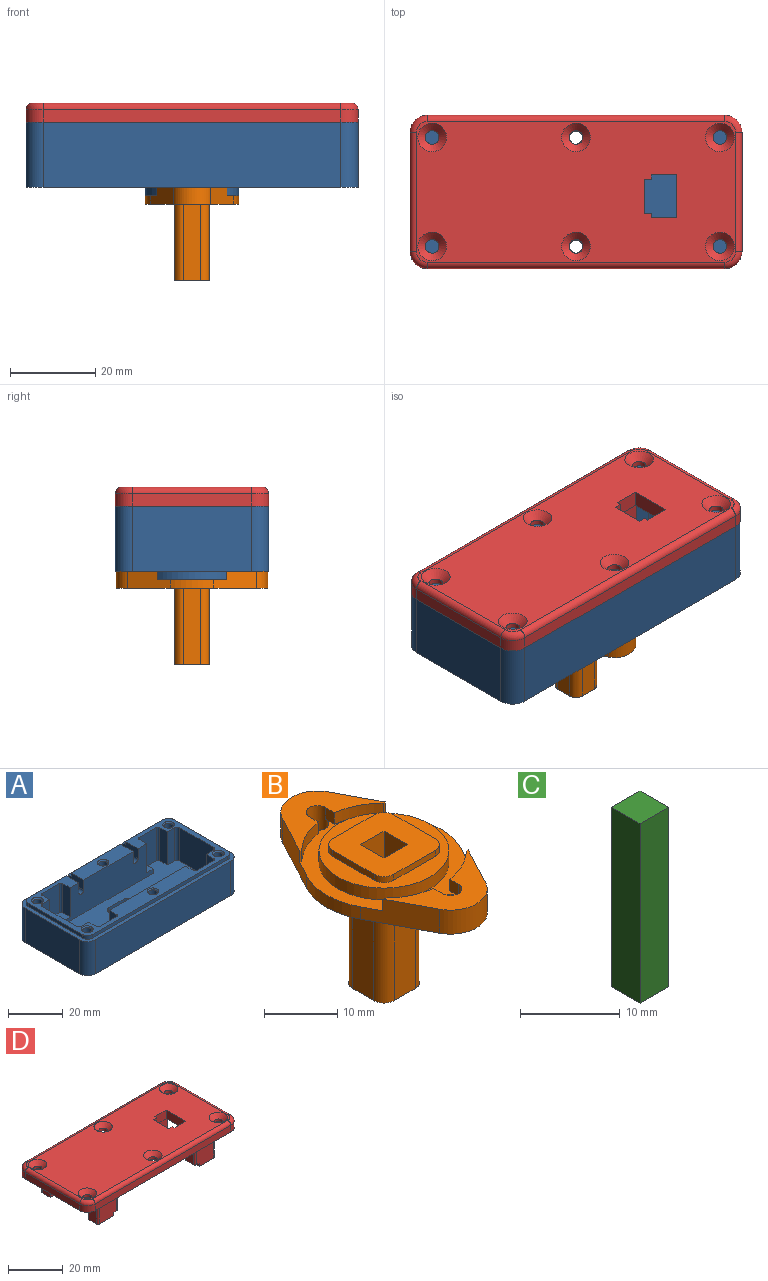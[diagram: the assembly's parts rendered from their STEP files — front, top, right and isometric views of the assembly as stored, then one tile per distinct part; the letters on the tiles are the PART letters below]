
ASSEMBLY  parts=4 mates=3
PART A: 98 faces, bbox 78x36x18.8 mm
  f0: plane 18x18mm, normal (0,0,-1), area 113.9mm2, adj f87,f88,f89,f90,f91,f92,f93,f94
  f1: plane 70.6x29.6mm, normal (0,0,1), area 1415.2mm2, adj f3,f4,f5,f6,f8,f17,f18,f19
  f2: plane 78x36mm, normal (0,0,-1), area 2397.5mm2, adj f53,f54,f55,f56,f57,f58,f59,f60
  f3: plane 46x14.8mm, normal (0,-1,0), area 567.6mm2, adj f1,f7,f13,f14,f15,f40,f41,f71
  f4: plane 14.8x3.7mm, normal (0,-1,0), area 54.8mm2, adj f1,f13,f18,f19
  f5: plane 14.8x3.7mm, normal (0,1,0), area 54.8mm2, adj f1,f13,f21,f23
  f6: plane 46x14.8mm, normal (0,1,0), area 595mm2, adj f1,f13,f16,f27,f28,f44,f83,f84
  f7: plane 25.5x6.45mm, normal (0,0,1), area 150.3mm2, adj f3,f10,f71,f76,f78
  f8: plane 14.8x3.7mm, normal (0,-1,0), area 54.8mm2, adj f1,f13,f35,f36
  f9: plane 19.75x1.5mm, normal (0,1,0), area 29.6mm2, adj f11,f13,f47,f74
  f10: plane 25.5x1.5mm, normal (0,1,0), area 38.2mm2, adj f7,f12,f71,f76
  f11: plane 78x36mm, normal (0,0,1), area 278.9mm2, adj f9,f45,f46,f47,f48,f49,f50,f51
  f12: plane 25.5x1.5mm, normal (0,0,1), area 38.2mm2, adj f10,f58,f71,f76
  f13: plane 75x33mm, normal (0,0,1), area 584.1mm2, adj f3,f4,f5,f6,f8,f9,f17,f18
  f14: plane 4.75x3.3mm, normal (0,0,1), area 15.5mm2, adj f3,f41,f42,f43,f86
  f15: plane 4.75x3.3mm, normal (0,0,1), area 15.5mm2, adj f3,f38,f39,f40,f85
  f16: plane 4.75x3.3mm, normal (0,0,1), area 15.5mm2, adj f6,f25,f26,f27,f84
  f17: cylinder r=0.8mm len=14.8mm, axis (0,0,1), area 18.6mm2, adj f1,f13,f18,f43
  f18: plane 14.8x3.95mm, normal (1,0,0), area 58.5mm2, adj f1,f4,f13,f17
  f19: cylinder r=1.3mm len=14.8mm, axis (0,0,1), area 30.2mm2, adj f1,f4,f13,f20
  f20: plane 17.5x14.8mm, normal (1,0,0), area 259mm2, adj f1,f13,f19,f21
  f21: cylinder r=1.3mm len=14.8mm, axis (0,0,1), area 30.2mm2, adj f1,f5,f13,f20
  f22: plane 14.8x3.7mm, normal (0,1,0), area 54.8mm2, adj f1,f13,f32,f33
  f23: plane 14.8x3.95mm, normal (1,0,0), area 58.5mm2, adj f1,f5,f13,f24
  f24: cylinder r=0.8mm len=14.8mm, axis (0,0,1), area 18.6mm2, adj f1,f13,f23,f25
  f25: plane 14.8x9mm, normal (0,1,0), area 128.7mm2, adj f1,f13,f16,f24,f26,f84
  f26: cylinder r=0.8mm len=13mm, axis (0,0,1), area 16.3mm2, adj f13,f16,f25,f27
  f27: plane 13x3.95mm, normal (-1,0,0), area 51.4mm2, adj f6,f13,f16,f26
  f28: plane 13x3.95mm, normal (1,0,0), area 51.4mm2, adj f6,f13,f29,f44
  f29: cylinder r=0.8mm len=13mm, axis (0,0,1), area 16.3mm2, adj f13,f28,f30,f44
  f30: plane 14.8x9mm, normal (0,1,0), area 128.7mm2, adj f1,f13,f29,f31,f44,f83
  f31: cylinder r=0.8mm len=14.8mm, axis (0,0,1), area 18.6mm2, adj f1,f13,f30,f32
  f32: plane 14.8x3.95mm, normal (-1,0,0), area 58.5mm2, adj f1,f13,f22,f31
  f33: cylinder r=1.3mm len=14.8mm, axis (0,0,1), area 30.2mm2, adj f1,f13,f22,f34
  f34: plane 17.5x14.8mm, normal (-1,0,0), area 259mm2, adj f1,f13,f33,f35
  f35: cylinder r=1.3mm len=14.8mm, axis (0,0,1), area 30.2mm2, adj f1,f8,f13,f34
  f36: plane 14.8x3.95mm, normal (-1,0,0), area 58.5mm2, adj f1,f8,f13,f37
  f37: cylinder r=0.8mm len=14.8mm, axis (0,0,1), area 18.6mm2, adj f1,f13,f36,f38
  f38: plane 14.8x9mm, normal (0,-1,0), area 128.7mm2, adj f1,f13,f15,f37,f39,f85
  f39: cylinder r=0.8mm len=13mm, axis (0,0,1), area 16.3mm2, adj f13,f15,f38,f40
  f40: plane 13x3.95mm, normal (1,0,0), area 51.4mm2, adj f3,f13,f15,f39
  f41: plane 13x3.95mm, normal (-1,0,0), area 51.4mm2, adj f3,f13,f14,f42
  f42: cylinder r=0.8mm len=13mm, axis (0,0,1), area 16.3mm2, adj f13,f14,f41,f43
  f43: plane 14.8x9mm, normal (0,-1,0), area 128.7mm2, adj f1,f13,f14,f17,f42,f86
  f44: plane 4.75x3.3mm, normal (0,0,1), area 15.5mm2, adj f6,f28,f29,f30,f83
  f45: cylinder r=2.5mm len=2.5mm, axis (0,0,1), area 5.9mm2, adj f11,f13,f46,f52
  f46: plane 19.75x1.5mm, normal (0,1,0), area 29.6mm2, adj f11,f13,f45,f73
  f47: cylinder r=2.5mm len=2.5mm, axis (0,0,1), area 5.9mm2, adj f9,f11,f13,f48
  f48: plane 28x1.5mm, normal (1,0,0), area 42mm2, adj f11,f13,f47,f49
  f49: cylinder r=2.5mm len=2.5mm, axis (0,0,1), area 5.9mm2, adj f11,f13,f48,f50
  f50: plane 70x1.5mm, normal (0,-1,0), area 105mm2, adj f11,f13,f49,f51
  f51: cylinder r=2.5mm len=2.5mm, axis (0,0,1), area 5.9mm2, adj f11,f13,f50,f52
  f52: plane 28x1.5mm, normal (-1,0,0), area 42mm2, adj f11,f13,f45,f51
  f53: cylinder r=4mm len=15.3mm, axis (0,0,-1), area 96.1mm2, adj f2,f11,f54,f60
  f54: plane 70x15.3mm, normal (0,-1,0), area 1071mm2, adj f2,f11,f53,f55
  f55: cylinder r=4mm len=15.3mm, axis (0,0,-1), area 96.1mm2, adj f2,f11,f54,f56
  f56: plane 28x15.3mm, normal (-1,0,0), area 428.4mm2, adj f2,f11,f55,f57
  f57: cylinder r=4mm len=15.3mm, axis (0,0,-1), area 96.1mm2, adj f2,f11,f56,f58
  f58: plane 70x15.3mm, normal (0,1,0), area 1051.1mm2, adj f2,f11,f12,f57,f59,f71,f72,f73
  f59: cylinder r=4mm len=15.3mm, axis (0,0,-1), area 96.1mm2, adj f2,f11,f58,f60
  f60: plane 28x15.3mm, normal (1,0,0), area 428.4mm2, adj f2,f11,f53,f59
  f61: cylinder r=1.62mm len=5.5mm, axis (0,0,1), area 56.2mm2, adj f62,f81
  f62: plane 3.25x3.25mm, normal (0,0,1), area 8.3mm2, adj f61
  f63: cylinder r=1.62mm len=5.5mm, axis (0,0,1), area 56.2mm2, adj f64,f82
  f64: plane 3.25x3.25mm, normal (0,0,1), area 8.3mm2, adj f63
  f65: cylinder r=1.62mm len=5.5mm, axis (0,0,1), area 56.2mm2, adj f66,f79
  f66: plane 3.25x3.25mm, normal (0,0,1), area 8.3mm2, adj f65
  f67: cylinder r=1.62mm len=5.5mm, axis (0,0,1), area 56.2mm2, adj f68,f80
  f68: plane 3.25x3.25mm, normal (0,0,1), area 8.3mm2, adj f67
  f69: cylinder r=1.62mm len=16.3mm, axis (0,0,1), area 166.4mm2, adj f2,f77
  f70: cylinder r=1.62mm len=16.3mm, axis (0,0,1), area 166.4mm2, adj f2,f78
  f71: plane 7.95x4.5mm, normal (-1,0,0), area 33.5mm2, adj f3,f7,f10,f12,f58,f72
  f72: cylinder r=1.25mm len=7.95mm, axis (0,1,0), area 31.2mm2, adj f3,f58,f71,f73
  f73: plane 7.95x4.5mm, normal (1,0,0), area 33.5mm2, adj f3,f11,f13,f46,f58,f72
  f74: plane 7.95x4.5mm, normal (-1,0,0), area 33.5mm2, adj f3,f9,f11,f13,f58,f75
  f75: cylinder r=1.25mm len=7.95mm, axis (0,1,0), area 31.2mm2, adj f3,f58,f74,f76
  f76: plane 7.95x4.5mm, normal (1,0,0), area 33.5mm2, adj f3,f7,f10,f12,f58,f75
  f77: cone r=1.62mm half-angle=45deg, axis (0,0,1), area 8.3mm2, adj f13,f69
  f78: cone r=1.62mm half-angle=45deg, axis (0,0,1), area 8.3mm2, adj f7,f70
  f79: cone r=1.62mm half-angle=45deg, axis (0,0,1), area 8.3mm2, adj f13,f65
  f80: cone r=1.62mm half-angle=45deg, axis (0,0,1), area 8.3mm2, adj f13,f67
  f81: cone r=1.62mm half-angle=45deg, axis (0,0,1), area 8.3mm2, adj f13,f61
  f82: cone r=1.62mm half-angle=45deg, axis (0,0,1), area 8.3mm2, adj f13,f63
  f83: plane 4.75x1.8mm, normal (1,0,0), area 8.6mm2, adj f1,f6,f30,f44
  f84: plane 4.75x1.8mm, normal (-1,0,0), area 8.6mm2, adj f1,f6,f16,f25
  f85: plane 4.75x1.8mm, normal (1,0,0), area 8.6mm2, adj f1,f3,f15,f38
  f86: plane 4.75x1.8mm, normal (-1,0,0), area 8.6mm2, adj f1,f3,f14,f43
  f87: plane 8x2mm, normal (0,1,0), area 16mm2, adj f0,f1,f88,f94
  f88: cylinder r=2mm len=2mm, axis (0,0,-1), area 6.3mm2, adj f0,f1,f87,f89
  f89: plane 8x2mm, normal (-1,0,0), area 16mm2, adj f0,f1,f88,f90
  f90: cylinder r=2mm len=2mm, axis (0,0,-1), area 6.3mm2, adj f0,f1,f89,f91
  f91: plane 8x2mm, normal (0,-1,0), area 16mm2, adj f0,f1,f90,f92
  f92: cylinder r=2mm len=2mm, axis (0,0,-1), area 6.3mm2, adj f0,f1,f91,f93
  f93: plane 8x2mm, normal (1,0,0), area 16mm2, adj f0,f1,f92,f94
  f94: cylinder r=2mm len=2mm, axis (0,0,-1), area 6.3mm2, adj f0,f1,f87,f93
  f95: cylinder r=9mm len=18mm, axis (0,0,1), area 113.1mm2, adj f0,f97
  f96: cylinder r=11mm len=22mm, axis (0,0,1), area 138.2mm2, adj f2,f97
  f97: plane 22x22mm, normal (0,0,-1), area 125.7mm2, adj f95,f96
PART B: 51 faces, bbox 22x35.6x23 mm
  f0: plane 16.42x9.8mm, normal (0,0,1), area 63.5mm2, adj f1,f6,f7,f39,f40,f41,f42,f46
  f1: cylinder r=11.2mm len=6.29mm, axis (0,0,1), area 13.9mm2, adj f0,f22,f40,f50
  f2: cylinder r=11.2mm len=6.29mm, axis (0,0,1), area 13.9mm2, adj f5,f22,f44,f47
  f3: cylinder r=1.55mm len=4mm, axis (0,0,-1), area 29.5mm2, adj f5,f11,f22,f47,f48
  f4: plane 9.99x5.3mm, normal (-0.88,-0.47,0), area 38.9mm2, adj f5,f10,f11,f22,f38,f44
  f5: plane 16.42x9.8mm, normal (0,0,1), area 63.5mm2, adj f2,f3,f4,f37,f38,f43,f44,f45
  f6: plane 9.99x5.3mm, normal (0.88,0.47,0), area 38.9mm2, adj f0,f8,f11,f22,f39,f40
  f7: plane 9.99x5.3mm, normal (-0.88,0.47,0), area 38.9mm2, adj f0,f10,f11,f22,f39,f42
  f8: cylinder r=11mm len=10.31mm, axis (0,0,1), area 22mm2, adj f6,f11,f22,f37
  f9: plane 11.8x11.8mm, normal (0,0,1), area 116.3mm2, adj f24,f25,f26,f27,f28,f29,f30,f31
  f10: cylinder r=11mm len=10.31mm, axis (0,0,1), area 22mm2, adj f4,f7,f11,f22
  f11: plane 35.6x22mm, normal (0,0,-1), area 458.4mm2, adj f3,f4,f6,f7,f8,f10,f12,f13
  f12: plane 18x4mm, normal (0,-1,0), area 72mm2, adj f11,f13,f19,f20
  f13: cylinder r=2mm len=18mm, axis (0,0,1), area 56.5mm2, adj f11,f12,f14,f20
  f14: plane 18x4mm, normal (-1,0,0), area 72mm2, adj f11,f13,f15,f20
  f15: cylinder r=2mm len=18mm, axis (0,0,1), area 56.5mm2, adj f11,f14,f16,f20
  f16: plane 18x4mm, normal (0,1,0), area 72mm2, adj f11,f15,f17,f20
  f17: cylinder r=2mm len=18mm, axis (0,0,1), area 56.5mm2, adj f11,f16,f18,f20
  f18: plane 18x4mm, normal (1,0,0), area 72mm2, adj f11,f17,f19,f20
  f19: cylinder r=2mm len=18mm, axis (0,0,1), area 56.5mm2, adj f11,f12,f18,f20
  f20: plane 8x8mm, normal (0,0,-1), area 60.6mm2, adj f12,f13,f14,f15,f16,f17,f18,f19
  f21: cylinder r=8.85mm len=17.7mm, axis (0,0,1), area 108.4mm2, adj f22,f23
  f22: plane 25.6x22mm, normal (0,0,1), area 145.8mm2, adj f1,f2,f3,f4,f6,f7,f8,f10
  f23: plane 17.7x17.7mm, normal (0,0,1), area 109.9mm2, adj f21,f24,f25,f26,f27,f28,f29,f30
  f24: plane 8x1mm, normal (-1,0,0), area 8mm2, adj f9,f23,f25,f31
  f25: cylinder r=1.9mm len=1.9mm, axis (0,0,-1), area 3mm2, adj f9,f23,f24,f26
  f26: plane 8x1mm, normal (0,-1,0), area 8mm2, adj f9,f23,f25,f27
  f27: cylinder r=1.9mm len=1.9mm, axis (0,0,-1), area 3mm2, adj f9,f23,f26,f28
  f28: plane 8x1mm, normal (1,0,0), area 8mm2, adj f9,f23,f27,f29
  f29: cylinder r=1.9mm len=1.9mm, axis (0,0,-1), area 3mm2, adj f9,f23,f28,f30
  f30: plane 8x1mm, normal (0,1,0), area 8mm2, adj f9,f23,f29,f31
  f31: cylinder r=1.9mm len=1.9mm, axis (0,0,-1), area 3mm2, adj f9,f23,f24,f30
  f32: plane 4.45x4.45mm, normal (0,0,1), area 19.8mm2, adj f33,f34,f35,f36
  f33: plane 21x4.45mm, normal (0,1,0), area 93.4mm2, adj f9,f32,f34,f36
  f34: plane 21x4.45mm, normal (-1,0,0), area 93.4mm2, adj f9,f32,f33,f35
  f35: plane 21x4.45mm, normal (0,-1,0), area 93.4mm2, adj f9,f32,f34,f36
  f36: plane 21x4.45mm, normal (1,0,0), area 93.4mm2, adj f9,f32,f33,f35
  f37: plane 9.99x5.3mm, normal (0.88,-0.47,0), area 38.9mm2, adj f5,f8,f11,f22,f38,f43
  f38: cylinder r=5mm len=8.83mm, axis (0,0,1), area 43.3mm2, adj f4,f5,f11,f37
  f39: cylinder r=5mm len=8.83mm, axis (0,0,1), area 43.3mm2, adj f0,f6,f7,f11
  f40: plane 1.95x0.37mm, normal (0,-1,0), area 0.7mm2, adj f0,f1,f6,f22
  f41: cylinder r=11.2mm len=6.29mm, axis (0,0,1), area 13.9mm2, adj f0,f22,f42,f49
  f42: plane 1.95x0.37mm, normal (0,-1,0), area 0.7mm2, adj f0,f7,f22,f41
  f43: plane 1.95x0.37mm, normal (0,1,0), area 0.7mm2, adj f5,f22,f37,f45
  f44: plane 1.95x0.37mm, normal (0,1,0), area 0.7mm2, adj f2,f4,f5,f22
  f45: cylinder r=11.2mm len=6.29mm, axis (0,0,1), area 13.9mm2, adj f5,f22,f43,f48
  f46: cylinder r=1.55mm len=4mm, axis (0,0,-1), area 29.5mm2, adj f0,f11,f22,f49,f50
  f47: plane 1.95x1.71mm, normal (1,0,0), area 3.3mm2, adj f2,f3,f5,f22
  f48: plane 1.95x1.71mm, normal (-1,0,0), area 3.3mm2, adj f3,f5,f22,f45
  f49: plane 1.95x1.71mm, normal (1,0,0), area 3.3mm2, adj f0,f22,f41,f46
  f50: plane 1.95x1.71mm, normal (-1,0,0), area 3.3mm2, adj f0,f1,f22,f46
PART C: 6 faces, bbox 4x4x22 mm
  f0: plane 22x4mm, normal (-1,0,0), area 88mm2, adj f1,f3,f4,f5
  f1: plane 22x4mm, normal (0,-1,0), area 88mm2, adj f0,f2,f4,f5
  f2: plane 22x4mm, normal (1,0,0), area 88mm2, adj f1,f3,f4,f5
  f3: plane 22x4mm, normal (0,1,0), area 88mm2, adj f0,f2,f4,f5
  f4: plane 4x4mm, normal (0,0,-1), area 16mm2, adj f0,f1,f2,f3
  f5: plane 4x4mm, normal (0,0,1), area 16mm2, adj f0,f1,f2,f3
PART D: 100 faces, bbox 78.7x36.7x15 mm
  f0: plane 70.4x19.9mm, normal (0,0,-1), area 1284.5mm2, adj f3,f4,f6,f7,f27,f29,f31,f32
  f1: plane 75x33mm, normal (0,0,1), area 2183.2mm2, adj f55,f56,f57,f58,f59,f60,f61,f62
  f2: plane 12x9mm, normal (0,1,0), area 105.7mm2, adj f11,f14,f26,f28,f86,f87
  f3: plane 10.5x5.05mm, normal (1,0,0), area 43mm2, adj f0,f10,f14,f26,f29,f53,f87
  f4: plane 10.5x5.05mm, normal (-1,0,0), area 43mm2, adj f0,f15,f26,f29,f49,f54,f89
  f5: plane 12x9mm, normal (0,1,0), area 105.7mm2, adj f15,f26,f30,f50,f88,f89
  f6: plane 10.5x5.05mm, normal (-1,0,0), area 43mm2, adj f0,f9,f16,f26,f40,f52,f91
  f7: plane 10.5x5.05mm, normal (1,0,0), area 43mm2, adj f0,f12,f17,f26,f40,f51,f85
  f8: plane 12x9mm, normal (0,-1,0), area 105.7mm2, adj f13,f17,f26,f41,f84,f85
  f9: plane 10.4x10.2mm, normal (0,1,0), area 102.8mm2, adj f6,f37,f48,f52,f90,f91
  f10: plane 10.4x10.2mm, normal (0,-1,0), area 102.8mm2, adj f3,f11,f27,f53,f86,f87
  f11: plane 8.2x4.75mm, normal (0,0,-1), area 38.8mm2, adj f2,f10,f27,f28,f86
  f12: plane 10.4x10.2mm, normal (0,1,0), area 102.8mm2, adj f7,f13,f42,f51,f84,f85
  f13: plane 8.2x4.75mm, normal (0,0,-1), area 38.8mm2, adj f8,f12,f41,f42,f84
  f14: cylinder r=0.7mm len=10.5mm, axis (0,0,1), area 11.5mm2, adj f2,f3,f26,f87
  f15: cylinder r=0.7mm len=10.5mm, axis (0,0,1), area 11.5mm2, adj f4,f5,f26,f89
  f16: cylinder r=0.7mm len=10.5mm, axis (0,0,1), area 11.5mm2, adj f6,f26,f39,f91
  f17: cylinder r=0.7mm len=10.5mm, axis (0,0,1), area 11.5mm2, adj f7,f8,f26,f85
  f18: cylinder r=4mm len=4mm, axis (0,0,1), area 18.8mm2, adj f19,f25,f61,f83
  f19: plane 70x3mm, normal (0,1,0), area 210mm2, adj f18,f20,f59,f83
  f20: cylinder r=4mm len=4mm, axis (0,0,1), area 18.8mm2, adj f19,f21,f57,f83
  f21: plane 28x3mm, normal (-1,0,0), area 84mm2, adj f20,f22,f55,f83
  f22: cylinder r=4mm len=4mm, axis (0,0,1), area 18.8mm2, adj f21,f23,f56,f83
  f23: plane 70x3mm, normal (0,-1,0), area 210mm2, adj f22,f24,f58,f83
  f24: cylinder r=4mm len=4mm, axis (0,0,1), area 18.8mm2, adj f23,f25,f60,f83
  f25: plane 28x3mm, normal (1,0,0), area 84mm2, adj f18,f24,f62,f83
  f26: plane 75.1x33.1mm, normal (0,0,-1), area 835.5mm2, adj f2,f3,f4,f5,f6,f7,f8,f14
  f27: plane 12x5.05mm, normal (-1,0,0), area 49.1mm2, adj f0,f10,f11,f26,f28,f47,f53
  f28: cylinder r=0.7mm len=12mm, axis (0,0,1), area 13.2mm2, adj f2,f11,f26,f27
  f29: plane 39.6x0.8mm, normal (0,1,0), area 31.7mm2, adj f0,f3,f4,f26
  f30: cylinder r=0.7mm len=12mm, axis (0,0,1), area 13.2mm2, adj f5,f26,f31,f50
  f31: plane 12x5.05mm, normal (1,0,0), area 49.1mm2, adj f0,f26,f30,f32,f49,f50,f54
  f32: plane 3.8x0.8mm, normal (0,1,0), area 3mm2, adj f0,f26,f31,f33
  f33: cylinder r=1.2mm len=1.2mm, axis (0,0,1), area 1.5mm2, adj f0,f26,f32,f34
  f34: plane 17.5x0.8mm, normal (1,0,0), area 14mm2, adj f0,f26,f33,f35
  f35: cylinder r=1.2mm len=1.2mm, axis (0,0,1), area 1.5mm2, adj f0,f26,f34,f36
  f36: plane 3.8x0.8mm, normal (0,-1,0), area 3mm2, adj f0,f26,f35,f37
  f37: plane 12x5.05mm, normal (1,0,0), area 49.1mm2, adj f0,f9,f26,f36,f38,f48,f52
  f38: cylinder r=0.7mm len=12mm, axis (0,0,1), area 13.2mm2, adj f26,f37,f39,f48
  f39: plane 12x9mm, normal (0,-1,0), area 105.7mm2, adj f16,f26,f38,f48,f90,f91
  f40: plane 39.6x0.8mm, normal (0,-1,0), area 31.7mm2, adj f0,f6,f7,f26
  f41: cylinder r=0.7mm len=12mm, axis (0,0,1), area 13.2mm2, adj f8,f13,f26,f42
  f42: plane 12x5.05mm, normal (-1,0,0), area 49.1mm2, adj f0,f12,f13,f26,f41,f43,f51
  f43: plane 3.8x0.8mm, normal (0,-1,0), area 3mm2, adj f0,f26,f42,f44
  f44: cylinder r=1.2mm len=1.2mm, axis (0,0,1), area 1.5mm2, adj f0,f26,f43,f45
  f45: plane 17.5x0.8mm, normal (-1,0,0), area 14mm2, adj f0,f26,f44,f46
  f46: cylinder r=1.2mm len=1.2mm, axis (0,0,1), area 1.5mm2, adj f0,f26,f45,f47
  f47: plane 3.8x0.8mm, normal (0,1,0), area 3mm2, adj f0,f26,f27,f46
  f48: plane 8.2x4.75mm, normal (0,0,-1), area 38.8mm2, adj f9,f37,f38,f39,f90
  f49: plane 10.4x10.2mm, normal (0,-1,0), area 102.8mm2, adj f4,f31,f50,f54,f88,f89
  f50: plane 8.2x4.75mm, normal (0,0,-1), area 38.8mm2, adj f5,f30,f31,f49,f88
  f51: plane 10.4x1mm, normal (0,0.71,-0.71), area 14.7mm2, adj f0,f7,f12,f42
  f52: plane 10.4x1mm, normal (0,0.71,-0.71), area 14.7mm2, adj f0,f6,f9,f37
  f53: plane 10.4x1mm, normal (0,-0.71,-0.71), area 14.7mm2, adj f0,f3,f10,f27
  f54: plane 10.4x1mm, normal (0,-0.71,-0.71), area 14.7mm2, adj f0,f4,f31,f49
  f55: cylinder r=1.5mm len=28mm, axis (0,-1,0), area 66mm2, adj f1,f21,f56,f57
  f56: torus R=2.5mm, axis (0,0,1), area 12.8mm2, adj f1,f22,f55,f58
  f57: torus R=2.5mm, axis (0,0,1), area 12.8mm2, adj f1,f20,f55,f59
  f58: cylinder r=1.5mm len=70mm, axis (1,0,0), area 164.9mm2, adj f1,f23,f56,f60
  f59: cylinder r=1.5mm len=70mm, axis (-1,0,0), area 164.9mm2, adj f1,f19,f57,f61
  f60: torus R=2.5mm, axis (0,0,1), area 12.8mm2, adj f1,f24,f58,f62
  f61: torus R=2.5mm, axis (0,0,1), area 12.8mm2, adj f1,f18,f59,f62
  f62: cylinder r=1.5mm len=28mm, axis (0,1,0), area 66mm2, adj f1,f25,f60,f61
  f63: cylinder r=1.6mm len=3.2mm, axis (0,0,1), area 12.5mm2, adj f26,f64
  f64: cone r=1.6mm half-angle=45deg, axis (0,0,1), area 38.8mm2, adj f1,f63
  f65: cylinder r=1.6mm len=3.2mm, axis (0,0,1), area 12.5mm2, adj f26,f66
  f66: cone r=1.6mm half-angle=45deg, axis (0,0,1), area 38.8mm2, adj f1,f65
  f67: cylinder r=1.6mm len=3.2mm, axis (0,0,1), area 12.5mm2, adj f26,f68
  f68: cone r=1.6mm half-angle=45deg, axis (0,0,1), area 38.8mm2, adj f1,f67
  f69: cylinder r=1.6mm len=3.2mm, axis (0,0,1), area 12.5mm2, adj f26,f70
  f70: cone r=1.6mm half-angle=45deg, axis (0,0,1), area 38.8mm2, adj f1,f69
  f71: cylinder r=1.6mm len=3.2mm, axis (0,0,1), area 12.5mm2, adj f26,f72
  f72: cone r=1.6mm half-angle=45deg, axis (0,0,1), area 38.8mm2, adj f1,f71
  f73: cylinder r=1.6mm len=3.2mm, axis (0,0,1), area 12.5mm2, adj f26,f74
  f74: cone r=1.6mm half-angle=45deg, axis (0,0,1), area 38.8mm2, adj f1,f73
  f75: cylinder r=2.55mm len=2.55mm, axis (0,0,1), area 6mm2, adj f26,f76,f82,f83
  f76: plane 70x1.5mm, normal (0,-1,0), area 105mm2, adj f26,f75,f77,f83
  f77: cylinder r=2.55mm len=2.55mm, axis (0,0,1), area 6mm2, adj f26,f76,f78,f83
  f78: plane 28x1.5mm, normal (1,0,0), area 42mm2, adj f26,f77,f79,f83
  f79: cylinder r=2.55mm len=2.55mm, axis (0,0,1), area 6mm2, adj f26,f78,f80,f83
  f80: plane 70x1.5mm, normal (0,1,0), area 105mm2, adj f26,f79,f81,f83
  f81: cylinder r=2.55mm len=2.55mm, axis (0,0,1), area 6mm2, adj f26,f80,f82,f83
  f82: plane 28x1.5mm, normal (-1,0,0), area 42mm2, adj f26,f75,f81,f83
  f83: plane 78x36mm, normal (0,0,-1), area 314mm2, adj f18,f19,f20,f21,f22,f23,f24,f25
  f84: plane 4.75x1.5mm, normal (1,0,0), area 7.1mm2, adj f8,f12,f13,f85
  f85: plane 4.75x2.2mm, normal (0,0,-1), area 10.3mm2, adj f7,f8,f12,f17,f84
  f86: plane 4.75x1.5mm, normal (1,0,0), area 7.1mm2, adj f2,f10,f11,f87
  f87: plane 4.75x2.2mm, normal (0,0,-1), area 10.3mm2, adj f2,f3,f10,f14,f86
  f88: plane 4.75x1.5mm, normal (-1,0,0), area 7.1mm2, adj f5,f49,f50,f89
  f89: plane 4.75x2.2mm, normal (0,0,-1), area 10.3mm2, adj f4,f5,f15,f49,f88
  f90: plane 4.75x1.5mm, normal (-1,0,0), area 7.1mm2, adj f9,f39,f48,f91
  f91: plane 4.75x2.2mm, normal (0,0,-1), area 10.3mm2, adj f6,f9,f16,f39,f90
  f92: plane 10x3.8mm, normal (-1,0,0), area 38mm2, adj f0,f1,f93,f99
  f93: plane 6x3.8mm, normal (0,-1,0), area 22.8mm2, adj f0,f1,f92,f94
  f94: plane 3.8x1mm, normal (1,0,0), area 3.8mm2, adj f0,f1,f93,f95
  f95: plane 3.8x1.7mm, normal (0,-1,0), area 6.5mm2, adj f0,f1,f94,f96
  f96: plane 8x3.8mm, normal (1,0,0), area 30.4mm2, adj f0,f1,f95,f97
  f97: plane 3.8x1.7mm, normal (0,1,0), area 6.5mm2, adj f0,f1,f96,f98
  f98: plane 3.8x1mm, normal (1,0,0), area 3.8mm2, adj f0,f1,f97,f99
  f99: plane 6x3.8mm, normal (0,1,0), area 22.8mm2, adj f0,f1,f92,f98
PLACE A t=(0.78,1.09,5.13)mm fixed
PLACE B t=(0.78,1.09,30.13)mm
PLACE C t=(0.78,1.09,5.58)mm
PLACE D rot(axis=(0,0,1),0deg) t=(0.78,1.09,-15.07)mm
MATE fastened C.f4 <-> B.f21  axis (0,0,-1) through (0.78,1.09,-14.87)mm
MATE fastened A.f96 <-> B.f2  axis (0,0,1) through (0.78,1.09,5.13)mm
MATE fastened A.f11 <-> D.f83  axis (0,0,1) through (39.78,1.09,20.43)mm
